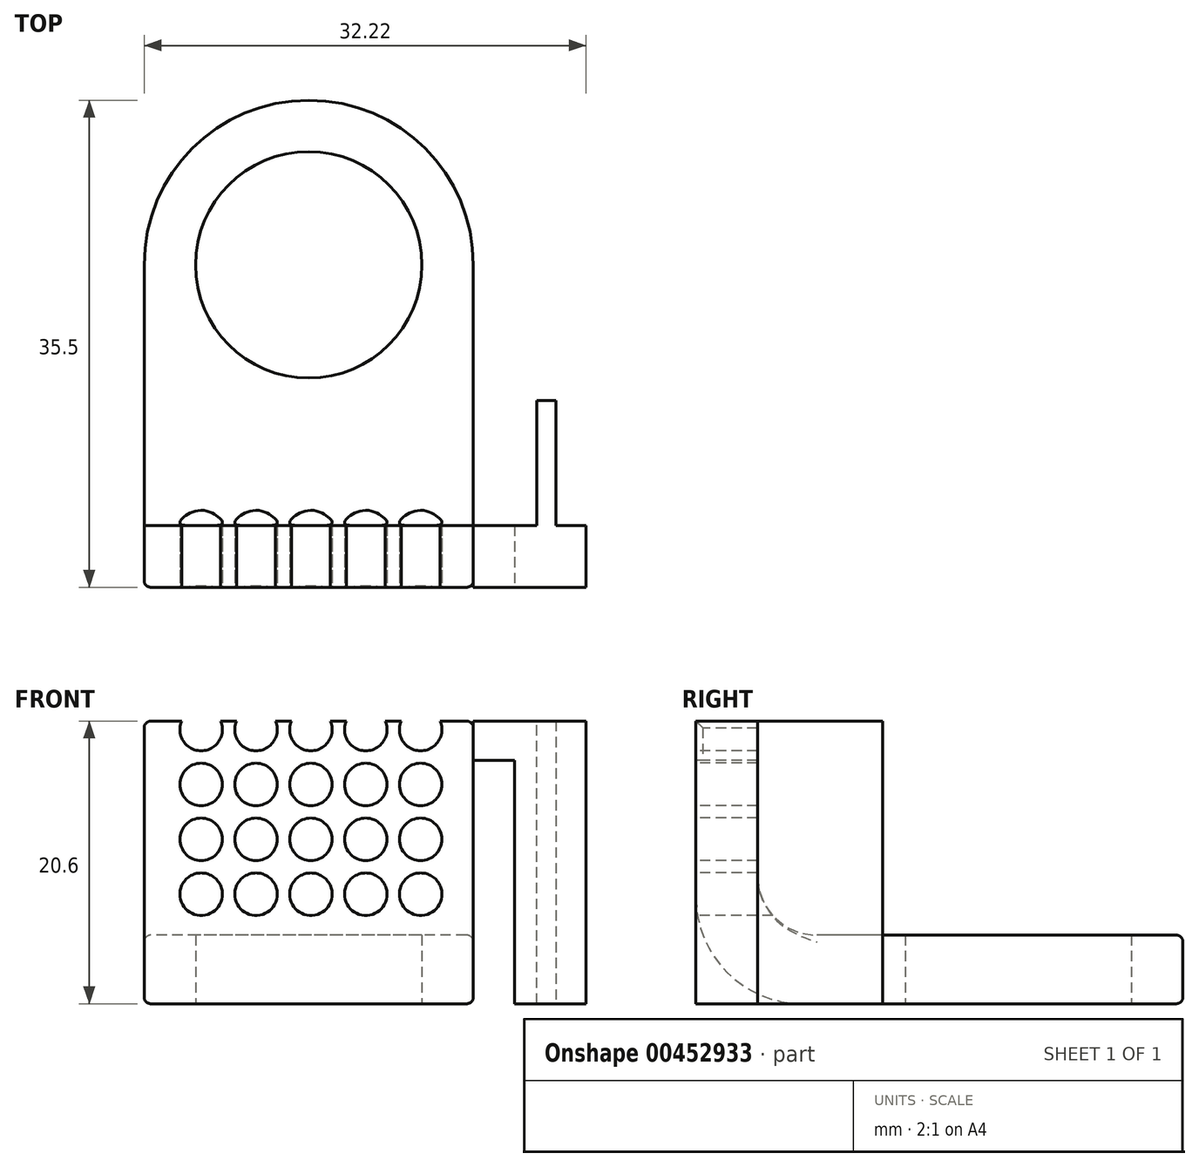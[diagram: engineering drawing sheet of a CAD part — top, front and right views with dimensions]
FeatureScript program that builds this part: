
annotation { "Feature Type Name" : "Feature", "Feature Type Description" : "" }
export const myFeature = defineFeature(function(context is Context, id is Id, definition is map)
    precondition{}
    {
        {
            var Q0;
            Q0=qCreatedBy(makeId("Top.planeOp"),FACE);
            var sketch = newSketch(context, id + "F0", { "sketchPlane" : qUnion([Q0])});
            skCircle(sketch, "E0", {"center": v(0, 0) * mm, "radius": 8.25 * mm});
            skCircle(sketch, "E1", {"center": v(0, 0) * mm, "radius": 12 * mm});
            skLineSegment(sketch, "E2", {"start": v(12, 0) * mm, "end": v(12, -23.5) * mm});
            skLineSegment(sketch, "E3", {"start": v(-12, 0) * mm, "end": v(-12, -23.5) * mm});
            skLineSegment(sketch, "E4", {"start": v(-12, -23.5) * mm, "end": v(12, -23.5) * mm});
            skPoint(sketch, "E5.orphan", {"position": v(-8.25, 0) * mm});
            skPoint(sketch, "E6.orphan", {"position": v(8.25, 0) * mm});
            skLineSegment(sketch, "E7", {"start": v(-12, -19) * mm, "end": v(12, -19) * mm});
            skSolve(sketch);
        }
        {
            var Q0;
            Q0=makeQuery(id+"F0.imprint","IMPRINT",FACE,{"disambiguationData":[TD([[makeQuery(id+"F0.imprint","IMPRINT",EDGE,{"derivedFrom":sQuery(id+"F0.wireOp",EDGE,"E0")}),-1.0]])]});
            var Q1;
            {var subQ0=sQuery(id+"F0.wireOp",EDGE,"E2");Q1=makeQuery(id+"F0.imprint","IMPRINT",FACE,{"disambiguationData":[TD([[makeQuery(id+"F0.imprint","IMPRINT",EDGE,{"derivedFrom":subQ0}),-1.0]])]});}
            extrude(context, id + "F1", {"entities" : qUnion([Q0, Q1]), "depth" : 5 * mm});
        }
        {
            var Q0;
            {var subQ0=sQuery(id+"F0.wireOp",EDGE,"E4");Q0=makeQuery(id+"F0.imprint","IMPRINT",FACE,{"disambiguationData":[TD([[makeQuery(id+"F0.imprint","IMPRINT",EDGE,{"derivedFrom":subQ0}),1.0]])]});}
            extrude(context, id + "F2", {"entities" : qUnion([Q0]), "operationType" : NewBodyOperationType.ADD, "depth" : 20.6 * mm});
        }
        {
            var Q0;
            {var subQ0=sQuery(id+"F0.wireOp",EDGE,"E4");Q0=makeQuery(id+"F2.boolean.opBoolean","MERGE",FACE,{"derivedFrom":[makeQuery(id+"F1.opExtrude","SWEPT_FACE",FACE,{"disambiguationData":[OSD([subQ0])]}),makeQuery(id+"F2.opExtrude","SWEPT_FACE",FACE,{"disambiguationData":[OSD([subQ0])]})]});}
            var sketch = newSketch(context, id + "F3", { "sketchPlane" : qUnion([Q0])});
            skLineSegment(sketch, "E8.bottom", {"start": v(15, 0) * mm, "end": v(20.22, 0) * mm});
            skLineSegment(sketch, "E8.top", {"start": v(15, 20.6) * mm, "end": v(20.22, 20.6) * mm});
            skLineSegment(sketch, "E8.left", {"start": v(15, 0) * mm, "end": v(15, 20.6) * mm});
            skLineSegment(sketch, "E8.right", {"start": v(20.22, 0) * mm, "end": v(20.22, 20.6) * mm});
            skLineSegment(sketch, "E9.bottom", {"start": v(12, 20.6) * mm, "end": v(15, 20.6) * mm});
            skLineSegment(sketch, "E9.top", {"start": v(12, 17.74) * mm, "end": v(15, 17.74) * mm});
            skLineSegment(sketch, "E9.left", {"start": v(12, 20.6) * mm, "end": v(12, 17.74) * mm});
            skLineSegment(sketch, "E9.right", {"start": v(15, 20.6) * mm, "end": v(15, 17.74) * mm});
            skLineSegment(sketch, "E10", {"start": v(18, 0) * mm, "end": v(18, 20.6) * mm});
            skPoint(sketch, "E10.endSnap0", {"position": v(17.6, 20.6) * mm});
            skLineSegment(sketch, "E11", {"start": v(18, 20.6) * mm, "end": v(16.63, 20.6) * mm});
            skLineSegment(sketch, "E12", {"start": v(16.63, 20.6) * mm, "end": v(16.63, 0) * mm});
            skCircle(sketch, "E13", {"center": v(-7.84, 7.98) * mm, "radius": 1.55 * mm});
            skCircle(sketch, "E14.0.1.0", {"center": v(-7.84, 11.98) * mm, "radius": 1.55 * mm});
            skCircle(sketch, "E14.0.2.0", {"center": v(-7.84, 15.98) * mm, "radius": 1.55 * mm});
            skCircle(sketch, "E14.0.3.0", {"center": v(-7.84, 19.98) * mm, "radius": 1.55 * mm});
            skCircle(sketch, "E14.1.0.0", {"center": v(-3.84, 7.98) * mm, "radius": 1.55 * mm});
            skCircle(sketch, "E14.1.1.0", {"center": v(-3.84, 11.98) * mm, "radius": 1.55 * mm});
            skCircle(sketch, "E14.1.2.0", {"center": v(-3.84, 15.98) * mm, "radius": 1.55 * mm});
            skCircle(sketch, "E14.1.3.0", {"center": v(-3.84, 19.98) * mm, "radius": 1.55 * mm});
            skCircle(sketch, "E14.2.0.0", {"center": v(0.16, 7.98) * mm, "radius": 1.55 * mm});
            skCircle(sketch, "E14.2.1.0", {"center": v(0.16, 11.98) * mm, "radius": 1.55 * mm});
            skCircle(sketch, "E14.2.2.0", {"center": v(0.16, 15.98) * mm, "radius": 1.55 * mm});
            skCircle(sketch, "E14.2.3.0", {"center": v(0.16, 19.98) * mm, "radius": 1.55 * mm});
            skCircle(sketch, "E14.3.0.0", {"center": v(4.16, 7.98) * mm, "radius": 1.55 * mm});
            skCircle(sketch, "E14.3.1.0", {"center": v(4.16, 11.98) * mm, "radius": 1.55 * mm});
            skCircle(sketch, "E14.3.2.0", {"center": v(4.16, 15.98) * mm, "radius": 1.55 * mm});
            skCircle(sketch, "E14.3.3.0", {"center": v(4.16, 19.98) * mm, "radius": 1.55 * mm});
            skCircle(sketch, "E14.4.0.0", {"center": v(8.16, 7.98) * mm, "radius": 1.55 * mm});
            skCircle(sketch, "E14.4.1.0", {"center": v(8.16, 11.98) * mm, "radius": 1.55 * mm});
            skCircle(sketch, "E14.4.2.0", {"center": v(8.16, 15.98) * mm, "radius": 1.55 * mm});
            skCircle(sketch, "E14.4.3.0", {"center": v(8.16, 19.98) * mm, "radius": 1.55 * mm});
            skLineSegment(sketch, "E14.direction1", {"start": v(-7.84, 7.98) * mm, "end": v(-3.84, 7.98) * mm, "construction": true});
            skLineSegment(sketch, "E14.direction2", {"start": v(-7.84, 7.98) * mm, "end": v(-7.84, 11.98) * mm, "construction": true});
            skSolve(sketch);
        }
        {
            var Q0;
            {var subQ12=sQuery(id+"F3.wireOp",EDGE,"E9.left");Q0=makeQuery(id+"F3.imprint","IMPRINT",FACE,{"disambiguationData":[TD([[makeQuery(id+"F3.imprint","IMPRINT",EDGE,{"derivedFrom":subQ12}),-1.0]])]});}
            var Q1;
            Q1=sQuery(id+"F3.wireOp",EDGE,"E13");
            var Q2;
            Q2=sQuery(id+"F3.wireOp",EDGE,"E14.1.0.0");
            var Q3;
            Q3=sQuery(id+"F3.wireOp",EDGE,"E14.2.0.0");
            var Q4;
            Q4=sQuery(id+"F3.wireOp",EDGE,"E14.3.0.0");
            var Q5;
            Q5=sQuery(id+"F3.wireOp",EDGE,"E14.4.0.0");
            var Q6;
            Q6=sQuery(id+"F3.wireOp",EDGE,"E14.4.1.0");
            var Q7;
            Q7=sQuery(id+"F3.wireOp",EDGE,"E14.3.1.0");
            var Q8;
            Q8=sQuery(id+"F3.wireOp",EDGE,"E14.2.1.0");
            var Q9;
            Q9=sQuery(id+"F3.wireOp",EDGE,"E14.1.1.0");
            var Q10;
            Q10=sQuery(id+"F3.wireOp",EDGE,"E14.0.1.0");
            var Q11;
            Q11=sQuery(id+"F3.wireOp",EDGE,"E14.0.2.0");
            var Q12;
            Q12=sQuery(id+"F3.wireOp",EDGE,"E14.1.2.0");
            var Q13;
            Q13=sQuery(id+"F3.wireOp",EDGE,"E14.2.2.0");
            var Q14;
            Q14=sQuery(id+"F3.wireOp",EDGE,"E14.3.2.0");
            var Q15;
            Q15=sQuery(id+"F3.wireOp",EDGE,"E14.4.2.0");
            var Q16;
            Q16=sQuery(id+"F3.wireOp",EDGE,"E14.4.3.0");
            var Q17;
            Q17=sQuery(id+"F3.wireOp",EDGE,"E14.3.3.0");
            var Q18;
            Q18=sQuery(id+"F3.wireOp",EDGE,"E14.2.3.0");
            var Q19;
            Q19=sQuery(id+"F3.wireOp",EDGE,"E14.1.3.0");
            var Q20;
            Q20=sQuery(id+"F3.wireOp",EDGE,"E14.0.3.0");
            extrude(context, id + "F4", {"entities" : qUnion([Q0]), "operationType" : NewBodyOperationType.INTERSECT, "surfaceEntities" : qUnion([Q1, Q2, Q3, Q4, Q5, Q6, Q7, Q8, Q9, Q10, Q11, Q12, Q13, Q14, Q15, Q16, Q17, Q18, Q19, Q20]), "endBound" : BoundingType.THROUGH_ALL, "oppositeDirection" : true, "depth" : 25 * mm});
        }
        {
            var Q0;
            {var subQ0=sQuery(id+"F0.wireOp",EDGE,"E4");var subQ1=sQuery(id+"F0.wireOp",EDGE,"E3");Q0=makeQuery(id+"F2.boolean.opBoolean","MERGE",EDGE,{"derivedFrom":[makeQuery(id+"F1.opExtrude","SWEPT_EDGE",EDGE,{"disambiguationData":[OSD([subQ1,subQ0])]}),makeQuery(id+"F2.opExtrude","SWEPT_EDGE",EDGE,{"disambiguationData":[OSD([subQ1,subQ0])]})]});}
            var Q1;
            {var subQ0=sQuery(id+"F0.wireOp",EDGE,"E4");var subQ1=sQuery(id+"F0.wireOp",EDGE,"E2");Q1=makeQuery(id+"F2.boolean.opBoolean","MERGE",EDGE,{"derivedFrom":[makeQuery(id+"F1.opExtrude","SWEPT_EDGE",EDGE,{"disambiguationData":[OSD([subQ1,subQ0])]}),makeQuery(id+"F2.opExtrude","SWEPT_EDGE",EDGE,{"disambiguationData":[OSD([subQ1,subQ0])]})]});}
            var Q2;
            Q2=makeQuery(id+"F2.opExtrude","CAP_EDGE",EDGE,{"disambiguationData":[OSD([sQuery(id+"F0.wireOp",EDGE,"E2")])],"isStart":false});
            var Q3;
            Q3=makeQuery(id+"F2.opExtrude","CAP_EDGE",EDGE,{"disambiguationData":[OSD([sQuery(id+"F0.wireOp",EDGE,"E3")])],"isStart":false});
            var Q4;
            Q4=makeQuery(id+"F1.opExtrude","CAP_EDGE",EDGE,{"disambiguationData":[OSD([sQuery(id+"F0.wireOp",EDGE,"E2")])],"isStart":true});
            var Q5;
            Q5=makeQuery(id+"F1.opExtrude","CAP_EDGE",EDGE,{"disambiguationData":[OSD([sQuery(id+"F0.wireOp",EDGE,"E2")])],"isStart":false});
            fillet(context, id + "F5", {"entities" : qUnion([Q0, Q1, Q2, Q3, Q4, Q5]), "radius" : 0.5 * mm, "tangentPropagation" : true, "allowEdgeOverflow" : false});
        }
        {
            var Q0;
            Q0=makeQuery(id+"F1.opExtrude","CAP_EDGE",EDGE,{"disambiguationData":[OSD([sQuery(id+"F0.wireOp",EDGE,"E4")])],"isStart":true});
            fillet(context, id + "F6", {"entities" : qUnion([Q0]), "radius" : 7.8 * mm, "tangentPropagation" : true, "allowEdgeOverflow" : false});
        }
        {
            var Q0;
            Q0=makeQuery(id+"F2.boolean.opBoolean","INTERSECT",EDGE,{"derivedFrom":[makeQuery(id+"F1.opExtrude","CAP_FACE",FACE,{"disambiguationData":[OSD([sQuery(id+"F0.wireOp",EDGE,"E0"),sQuery(id+"F0.wireOp",EDGE,"E1"),sQuery(id+"F0.wireOp",EDGE,"E2"),sQuery(id+"F0.wireOp",EDGE,"E3"),sQuery(id+"F0.wireOp",EDGE,"E4")])],"isStart":false}),makeQuery(id+"F2.opExtrude","SWEPT_FACE",FACE,{"disambiguationData":[OSD([sQuery(id+"F0.wireOp",EDGE,"E7")])]})]});
            fillet(context, id + "F7", {"entities" : qUnion([Q0]), "radius" : 4.32 * mm, "tangentPropagation" : true, "allowEdgeOverflow" : false});
        }
        {
            var Q0;
            Q0=makeQuery(id+"F3.imprint","IMPRINT",FACE,{"disambiguationData":[TD([[makeQuery(id+"F3.imprint","IMPRINT",EDGE,{"derivedFrom":sQuery(id+"F3.wireOp",EDGE,"E8.bottom")}),1.0]])]});
            var Q1;
            Q1=makeQuery(id+"F3.imprint","IMPRINT",FACE,{"disambiguationData":[TD([[makeQuery(id+"F3.imprint","IMPRINT",EDGE,{"derivedFrom":sQuery(id+"F3.wireOp",EDGE,"E9.bottom")}),-1.0]])]});
            var Q2;
            {var subQ3=sQuery(id+"F3.wireOp",EDGE,"E8.left");Q2=makeQuery(id+"F3.imprint","IMPRINT",FACE,{"disambiguationData":[TD([[makeQuery(id+"F3.imprint","IMPRINT",EDGE,{"derivedFrom":subQ3}),-1.0]])]});}
            var Q3;
            Q3=makeQuery(id+"F2.opExtrude","SWEPT_FACE",FACE,{"disambiguationData":[OSD([sQuery(id+"F0.wireOp",EDGE,"E7")])]});
            extrude(context, id + "F8", {"entities" : qUnion([Q0, Q1, Q2]), "operationType" : NewBodyOperationType.ADD, "endBound" : BoundingType.UP_TO_SURFACE, "oppositeDirection" : true, "endBoundEntityFace" : qUnion([Q3]), "depth" : 2.8 * mm});
        }
        {
            var Q0;
            {var subQ0=sQuery(id+"F3.wireOp",EDGE,"E10");Q0=makeQuery(id+"F3.imprint","IMPRINT",FACE,{"disambiguationData":[TD([[makeQuery(id+"F3.imprint","IMPRINT",EDGE,{"derivedFrom":subQ0}),1.0]])]});}
            extrude(context, id + "F9", {"entities" : qUnion([Q0]), "operationType" : NewBodyOperationType.ADD, "oppositeDirection" : true, "depth" : 13.6 * mm});
        }
    });
